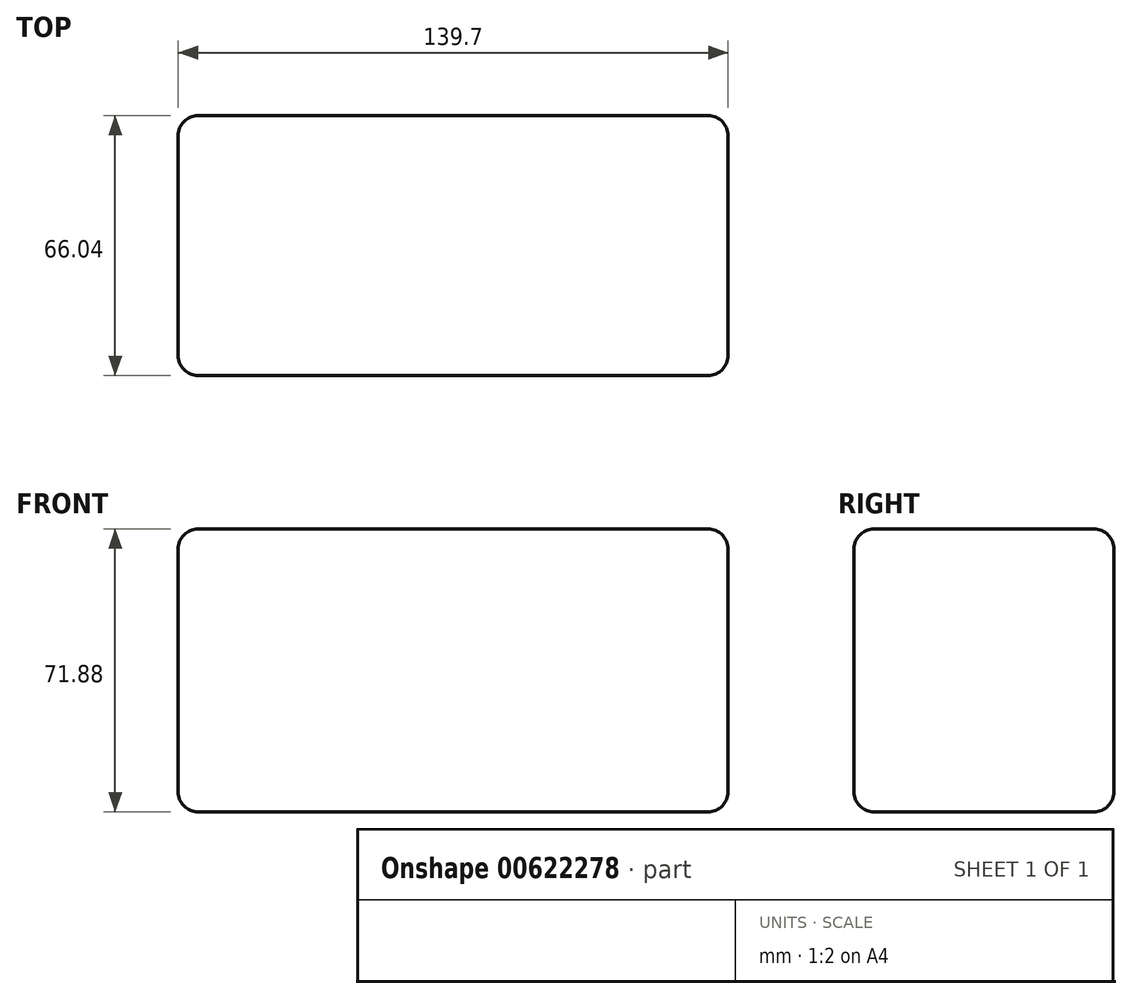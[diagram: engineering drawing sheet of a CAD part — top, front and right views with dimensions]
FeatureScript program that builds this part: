
annotation { "Feature Type Name" : "Feature", "Feature Type Description" : "" }
export const myFeature = defineFeature(function(context is Context, id is Id, definition is map)
    precondition{}
    {
        {
            var Q0;
            Q0=qCreatedBy(makeId("Top.planeOp"),FACE);
            var sketch = newSketch(context, id + "F0", { "sketchPlane" : qUnion([Q0])});
            skLineSegment(sketch, "E0.bottom", {"start": v(-127.1, 7.8) * mm, "end": v(12.6, 7.8) * mm});
            skLineSegment(sketch, "E0.top", {"start": v(-127.1, -58.24) * mm, "end": v(12.6, -58.24) * mm});
            skLineSegment(sketch, "E0.left", {"start": v(-127.1, 7.8) * mm, "end": v(-127.1, -58.24) * mm});
            skLineSegment(sketch, "E0.right", {"start": v(12.6, 7.8) * mm, "end": v(12.6, -58.24) * mm});
            skSolve(sketch);
        }
        {
            var Q0;
            Q0=makeQuery(id+"F0.imprint","IMPRINT",FACE,{"disambiguationData":[TD([[makeQuery(id+"F0.imprint","IMPRINT",EDGE,{"derivedFrom":sQuery(id+"F0.wireOp",EDGE,"E0.bottom")}),-1.0]])]});
            extrude(context, id + "F1", {"entities" : qUnion([Q0]), "depth" : 40.64 * mm, "offsetDistance" : 25.4 * mm});
        }
        {
            var Q0;
            Q0=makeQuery(id+"F1.opExtrude","CAP_FACE",FACE,{"disambiguationData":[OSD([sQuery(id+"F0.wireOp",EDGE,"E0.bottom"),sQuery(id+"F0.wireOp",EDGE,"E0.top"),sQuery(id+"F0.wireOp",EDGE,"E0.left"),sQuery(id+"F0.wireOp",EDGE,"E0.right")])],"isStart":false});
            var sketch = newSketch(context, id + "F2", { "sketchPlane" : qUnion([Q0])});
            skLineSegment(sketch, "E1.bottom", {"start": v(-127.1, 7.8) * mm, "end": v(-106.79, 7.8) * mm});
            skLineSegment(sketch, "E1.top", {"start": v(-127.1, -58.24) * mm, "end": v(-106.79, -58.24) * mm});
            skLineSegment(sketch, "E1.left", {"start": v(-127.1, 7.8) * mm, "end": v(-127.1, -58.24) * mm});
            skLineSegment(sketch, "E1.right", {"start": v(-106.79, 7.8) * mm, "end": v(-106.79, -58.24) * mm});
            skLineSegment(sketch, "E2", {"start": v(-57.26, 7.8) * mm, "end": v(-57.26, -58.24) * mm, "construction": true});
            skLineSegment(sketch, "E3.MirrorCS", {"start": v(-7.73, 7.8) * mm, "end": v(-7.73, -58.24) * mm});
            skLineSegment(sketch, "E4.MirrorCS", {"start": v(12.6, 7.8) * mm, "end": v(-7.73, 7.8) * mm});
            skLineSegment(sketch, "E5.MirrorCS", {"start": v(12.6, 7.8) * mm, "end": v(12.6, -58.24) * mm});
            skLineSegment(sketch, "E6.MirrorCS", {"start": v(12.6, -58.24) * mm, "end": v(-7.73, -58.24) * mm});
            skLineSegment(sketch, "E7.bottom", {"start": v(-106.79, -58.24) * mm, "end": v(-7.73, -58.24) * mm});
            skLineSegment(sketch, "E7.top", {"start": v(-106.79, -30.3) * mm, "end": v(-7.73, -30.3) * mm});
            skLineSegment(sketch, "E7.left", {"start": v(-106.79, -58.24) * mm, "end": v(-106.79, -30.3) * mm});
            skLineSegment(sketch, "E7.right", {"start": v(-7.73, -58.24) * mm, "end": v(-7.73, -30.3) * mm});
            skSolve(sketch);
        }
        {
            var Q0;
            Q0=makeQuery(id+"F2.imprint","IMPRINT",FACE,{"disambiguationData":[TD([[makeQuery(id+"F2.imprint","IMPRINT",EDGE,{"derivedFrom":sQuery(id+"F2.wireOp",EDGE,"E1.bottom")}),-1.0]])]});
            var Q1;
            Q1=makeQuery(id+"F2.imprint","IMPRINT",FACE,{"disambiguationData":[TD([[makeQuery(id+"F2.imprint","IMPRINT",EDGE,{"derivedFrom":sQuery(id+"F2.wireOp",EDGE,"E3.MirrorCS")}),1.0]])]});
            var Q2;
            {var subQ0=sQuery(id+"F2.wireOp",EDGE,"E1.right");Q2=makeQuery(id+"F2.imprint","IMPRINT",FACE,{"disambiguationData":[TD([[makeQuery(id+"F2.imprint","IMPRINT",EDGE,{"derivedFrom":subQ0}),1.0]])]});}
            extrude(context, id + "F3", {"entities" : qUnion([Q0, Q1, Q2]), "operationType" : NewBodyOperationType.ADD, "depth" : 31.24 * mm, "offsetDistance" : 25.4 * mm});
        }
        {
            var Q0;
            Q0=makeQuery(id+"F3.opExtrude","CAP_EDGE",EDGE,{"disambiguationData":[OSD([sQuery(id+"F2.wireOp",EDGE,"E7.top")])],"isStart":false});
            var Q1;
            Q1=makeQuery(id+"F3.opExtrude","CAP_EDGE",EDGE,{"disambiguationData":[OSD([sQuery(id+"F2.wireOp",EDGE,"E7.right")])],"isStart":false});
            var Q2;
            Q2=makeQuery(id+"F3.opExtrude","CAP_EDGE",EDGE,{"disambiguationData":[OSD([sQuery(id+"F2.wireOp",EDGE,"E7.left")])],"isStart":false});
            var Q3;
            Q3=makeQuery(id+"F3.opExtrude","CAP_EDGE",EDGE,{"disambiguationData":[OSD([sQuery(id+"F2.wireOp",EDGE,"E6.MirrorCS")])],"isStart":false});
            var Q4;
            Q4=makeQuery(id+"F3.opExtrude","CAP_EDGE",EDGE,{"disambiguationData":[OSD([sQuery(id+"F2.wireOp",EDGE,"E5.MirrorCS")])],"isStart":false});
            var Q5;
            Q5=makeQuery(id+"F3.opExtrude","CAP_EDGE",EDGE,{"disambiguationData":[OSD([sQuery(id+"F2.wireOp",EDGE,"E1.top")])],"isStart":false});
            var Q6;
            Q6=makeQuery(id+"F3.opExtrude","CAP_EDGE",EDGE,{"disambiguationData":[OSD([sQuery(id+"F2.wireOp",EDGE,"E1.left")])],"isStart":false});
            var Q7;
            Q7=makeQuery(id+"F3.opExtrude","CAP_EDGE",EDGE,{"disambiguationData":[OSD([sQuery(id+"F0.wireOp",EDGE,"E0.bottom"),sQuery(id+"F2.wireOp",EDGE,"E1.bottom"),sQuery(id+"F2.wireOp",EDGE,"E4.MirrorCS")])],"isStart":false});
            var Q8;
            Q8=makeQuery(id+"F3.boolean.opBoolean","MERGE",EDGE,{"derivedFrom":[makeQuery(id+"F1.opExtrude","SWEPT_EDGE",EDGE,{"disambiguationData":[OSD([sQuery(id+"F0.wireOp",EDGE,"E0.top"),sQuery(id+"F0.wireOp",EDGE,"E0.right")])]}),makeQuery(id+"F3.opExtrude","SWEPT_EDGE",EDGE,{"disambiguationData":[OSD([sQuery(id+"F2.wireOp",EDGE,"E5.MirrorCS"),sQuery(id+"F2.wireOp",EDGE,"E6.MirrorCS")])]})]});
            var Q9;
            Q9=makeQuery(id+"F3.opExtrude","SWEPT_EDGE",EDGE,{"disambiguationData":[OSD([sQuery(id+"F2.wireOp",EDGE,"E6.MirrorCS"),sQuery(id+"F2.wireOp",EDGE,"E7.bottom"),sQuery(id+"F2.wireOp",EDGE,"E7.right")])]});
            var Q10;
            Q10=makeQuery(id+"F1.opExtrude","CAP_EDGE",EDGE,{"disambiguationData":[OSD([sQuery(id+"F0.wireOp",EDGE,"E0.top")])],"isStart":false});
            var Q11;
            Q11=makeQuery(id+"F3.opExtrude","CAP_EDGE",EDGE,{"disambiguationData":[OSD([sQuery(id+"F2.wireOp",EDGE,"E7.top")])],"isStart":true});
            var Q12;
            Q12=makeQuery(id+"F3.opExtrude","SWEPT_EDGE",EDGE,{"disambiguationData":[OSD([sQuery(id+"F2.wireOp",EDGE,"E1.top"),sQuery(id+"F2.wireOp",EDGE,"E7.bottom"),sQuery(id+"F2.wireOp",EDGE,"E7.left")])]});
            var Q13;
            Q13=makeQuery(id+"F3.boolean.opBoolean","MERGE",EDGE,{"derivedFrom":[makeQuery(id+"F1.opExtrude","SWEPT_EDGE",EDGE,{"disambiguationData":[OSD([sQuery(id+"F0.wireOp",EDGE,"E0.top"),sQuery(id+"F0.wireOp",EDGE,"E0.left")])]}),makeQuery(id+"F3.opExtrude","SWEPT_EDGE",EDGE,{"disambiguationData":[OSD([sQuery(id+"F2.wireOp",EDGE,"E1.top"),sQuery(id+"F2.wireOp",EDGE,"E1.left")])]})]});
            var Q14;
            Q14=makeQuery(id+"F3.boolean.opBoolean","MERGE",FACE,{"derivedFrom":[makeQuery(id+"F1.opExtrude","SWEPT_FACE",FACE,{"disambiguationData":[OSD([sQuery(id+"F0.wireOp",EDGE,"E0.top")])]}),makeQuery(id+"F3.opExtrude","SWEPT_FACE",FACE,{"disambiguationData":[OSD([sQuery(id+"F2.wireOp",EDGE,"E1.top")])]}),makeQuery(id+"F3.opExtrude","SWEPT_FACE",FACE,{"disambiguationData":[OSD([sQuery(id+"F2.wireOp",EDGE,"E6.MirrorCS")])]})]});
            var Q15;
            Q15=makeQuery(id+"F1.opExtrude","CAP_EDGE",EDGE,{"disambiguationData":[OSD([sQuery(id+"F0.wireOp",EDGE,"E0.left")])],"isStart":true});
            var Q16;
            Q16=makeQuery(id+"F1.opExtrude","CAP_EDGE",EDGE,{"disambiguationData":[OSD([sQuery(id+"F0.wireOp",EDGE,"E0.top")])],"isStart":true});
            var Q17;
            Q17=makeQuery(id+"F1.opExtrude","CAP_EDGE",EDGE,{"disambiguationData":[OSD([sQuery(id+"F0.wireOp",EDGE,"E0.bottom")])],"isStart":true});
            var Q18;
            Q18=makeQuery(id+"F3.boolean.opBoolean","MERGE",EDGE,{"derivedFrom":[makeQuery(id+"F1.opExtrude","SWEPT_EDGE",EDGE,{"disambiguationData":[OSD([sQuery(id+"F0.wireOp",EDGE,"E0.bottom"),sQuery(id+"F0.wireOp",EDGE,"E0.left")])]}),makeQuery(id+"F3.opExtrude","SWEPT_EDGE",EDGE,{"disambiguationData":[OSD([sQuery(id+"F2.wireOp",EDGE,"E1.bottom"),sQuery(id+"F2.wireOp",EDGE,"E1.left")])]})]});
            var Q19;
            Q19=makeQuery(id+"F3.boolean.opBoolean","MERGE",EDGE,{"derivedFrom":[makeQuery(id+"F1.opExtrude","SWEPT_EDGE",EDGE,{"disambiguationData":[OSD([sQuery(id+"F0.wireOp",EDGE,"E0.bottom"),sQuery(id+"F0.wireOp",EDGE,"E0.right")])]}),makeQuery(id+"F3.opExtrude","SWEPT_EDGE",EDGE,{"disambiguationData":[OSD([sQuery(id+"F2.wireOp",EDGE,"E4.MirrorCS"),sQuery(id+"F2.wireOp",EDGE,"E5.MirrorCS")])]})]});
            var Q20;
            Q20=makeQuery(id+"F1.opExtrude","CAP_EDGE",EDGE,{"disambiguationData":[OSD([sQuery(id+"F0.wireOp",EDGE,"E0.right")])],"isStart":true});
            fillet(context, id + "F4", {"entities" : qUnion([Q0, Q1, Q2, Q3, Q4, Q5, Q6, Q7, Q8, Q9, Q10, Q11, Q12, Q13, Q14, Q15, Q16, Q17, Q18, Q19, Q20]), "radius" : 5.08 * mm, "tangentPropagation" : true, "allowEdgeOverflow" : false});
        }
    });
